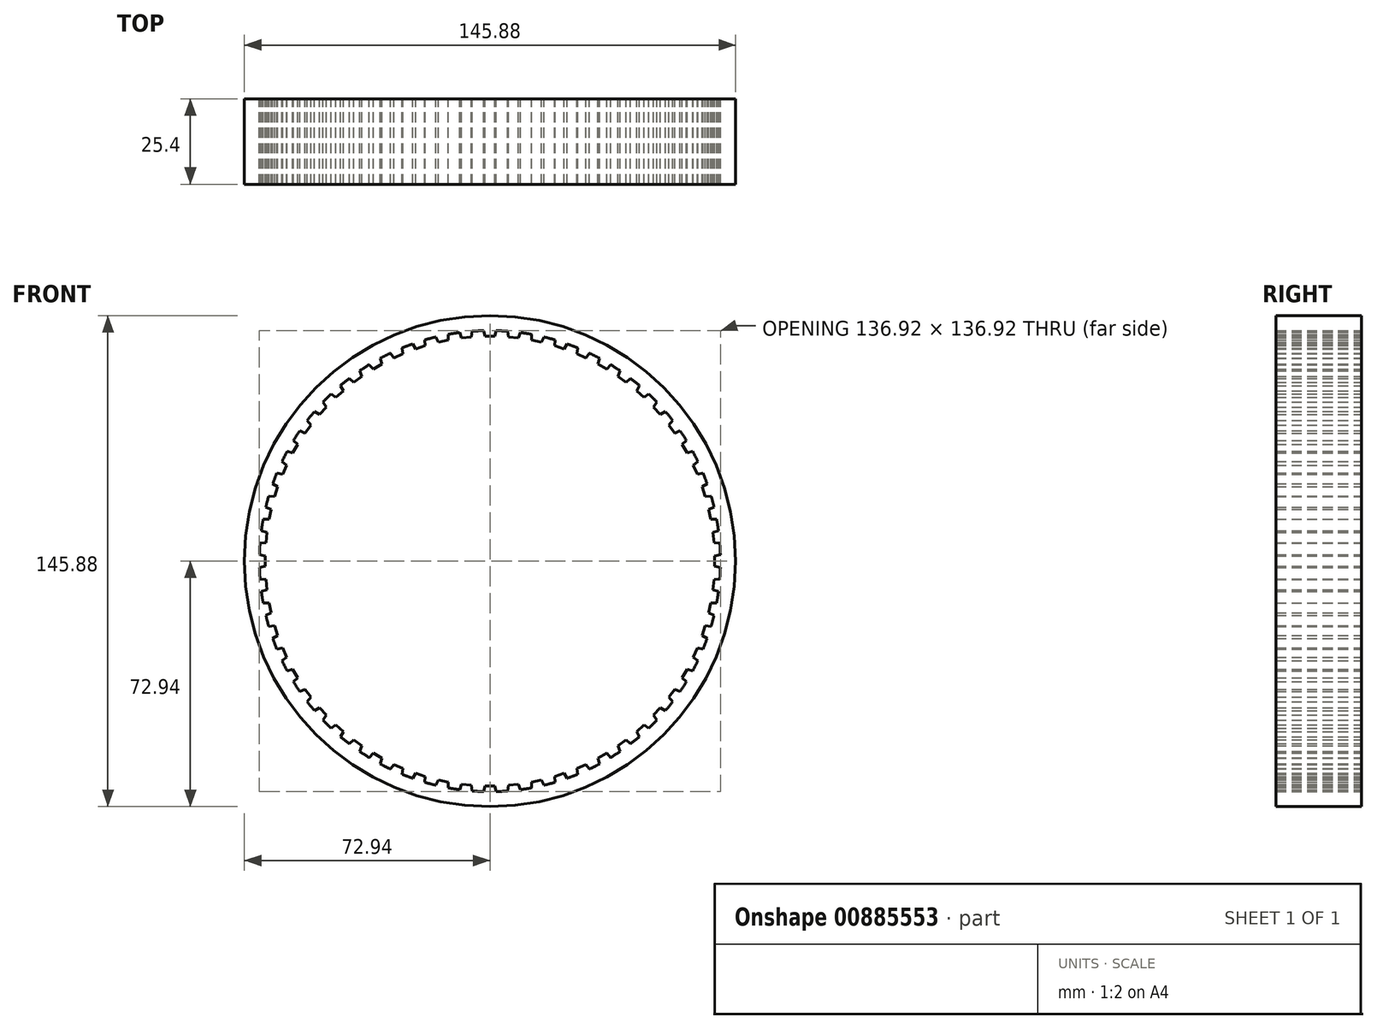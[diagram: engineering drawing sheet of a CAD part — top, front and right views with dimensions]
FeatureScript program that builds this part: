
annotation { "Feature Type Name" : "Feature", "Feature Type Description" : "" }
export const myFeature = defineFeature(function(context is Context, id is Id, definition is map)
    precondition{}
    {
        {
            var Q0;
            Q0=qCreatedBy(makeId("Front.planeOp"),FACE);
            var sketch = newSketch(context, id + "F0", { "sketchPlane" : qUnion([Q0])});
            skCircle(sketch, "E0", {"center": v(0, 0) * mm, "radius": 73.43 * mm});
            skLineSegment(sketch, "E1", {"start": v(0, 94.36) * mm, "end": v(0, -101.38) * mm, "construction": true});
            skLineSegment(sketch, "E2", {"start": v(-1.88, 68.46) * mm, "end": v(-1.48, 66.76) * mm});
            skLineSegment(sketch, "E3", {"start": v(-1.48, 66.76) * mm, "end": v(1.48, 66.76) * mm});
            skLineSegment(sketch, "E4", {"start": v(1.48, 66.76) * mm, "end": v(1.88, 68.46) * mm});
            skLineSegment(sketch, "E5", {"start": v(-8.37, 68.46) * mm, "end": v(10.76, 68.46) * mm, "construction": true});
            skLineSegment(sketch, "E6.1.0", {"start": v(-9.02, 67.89) * mm, "end": v(-8.45, 66.24) * mm});
            skLineSegment(sketch, "E6.1.1", {"start": v(-8.45, 66.24) * mm, "end": v(-5.5, 66.55) * mm});
            skLineSegment(sketch, "E6.1.2", {"start": v(-5.5, 66.55) * mm, "end": v(-5.29, 68.28) * mm});
            skLineSegment(sketch, "E6.2.0", {"start": v(-16.07, 66.57) * mm, "end": v(-15.33, 65) * mm});
            skLineSegment(sketch, "E6.2.1", {"start": v(-15.33, 65) * mm, "end": v(-12.43, 65.61) * mm});
            skLineSegment(sketch, "E6.2.2", {"start": v(-12.43, 65.61) * mm, "end": v(-12.4, 67.35) * mm});
            skLineSegment(sketch, "E7.2.3.0", {"start": v(-22.94, 64.53) * mm, "end": v(-22.04, 63.04) * mm});
            skLineSegment(sketch, "E7.3.3.0", {"start": v(-22.04, 63.04) * mm, "end": v(-19.22, 63.95) * mm});
            skLineSegment(sketch, "E7.6.3.0", {"start": v(-19.22, 63.95) * mm, "end": v(-19.37, 65.69) * mm});
            skLineSegment(sketch, "E7.2.4.0", {"start": v(-29.56, 61.78) * mm, "end": v(-28.51, 60.39) * mm});
            skLineSegment(sketch, "E7.3.4.0", {"start": v(-28.51, 60.39) * mm, "end": v(-25.8, 61.6) * mm});
            skLineSegment(sketch, "E7.6.4.0", {"start": v(-25.8, 61.6) * mm, "end": v(-26.13, 63.3) * mm});
            skLineSegment(sketch, "E7.2.5.0", {"start": v(-35.86, 58.35) * mm, "end": v(-34.67, 57.07) * mm});
            skLineSegment(sketch, "E7.3.5.0", {"start": v(-34.67, 57.07) * mm, "end": v(-32.1, 58.56) * mm});
            skLineSegment(sketch, "E7.6.5.0", {"start": v(-32.1, 58.56) * mm, "end": v(-32.6, 60.23) * mm});
            skLineSegment(sketch, "E7.2.6.0", {"start": v(-41.76, 54.28) * mm, "end": v(-40.44, 53.14) * mm});
            skLineSegment(sketch, "E7.3.6.0", {"start": v(-40.44, 53.14) * mm, "end": v(-38.04, 54.88) * mm});
            skLineSegment(sketch, "E7.6.6.0", {"start": v(-38.04, 54.88) * mm, "end": v(-38.72, 56.49) * mm});
            skLineSegment(sketch, "E7.2.7.0", {"start": v(-47.2, 49.62) * mm, "end": v(-45.77, 48.62) * mm});
            skLineSegment(sketch, "E7.3.7.0", {"start": v(-45.77, 48.62) * mm, "end": v(-43.57, 50.6) * mm});
            skLineSegment(sketch, "E7.6.7.0", {"start": v(-43.57, 50.6) * mm, "end": v(-44.41, 52.13) * mm});
            skLineSegment(sketch, "E7.2.8.0", {"start": v(-52.13, 44.41) * mm, "end": v(-50.6, 43.57) * mm});
            skLineSegment(sketch, "E7.3.8.0", {"start": v(-50.6, 43.57) * mm, "end": v(-48.62, 45.77) * mm});
            skLineSegment(sketch, "E7.6.8.0", {"start": v(-48.62, 45.77) * mm, "end": v(-49.62, 47.2) * mm});
            skLineSegment(sketch, "E7.2.9.0", {"start": v(-56.49, 38.72) * mm, "end": v(-54.88, 38.04) * mm});
            skLineSegment(sketch, "E7.3.9.0", {"start": v(-54.88, 38.04) * mm, "end": v(-53.14, 40.44) * mm});
            skLineSegment(sketch, "E7.6.9.0", {"start": v(-53.14, 40.44) * mm, "end": v(-54.28, 41.76) * mm});
            skLineSegment(sketch, "E7.2.10.0", {"start": v(-60.23, 32.6) * mm, "end": v(-58.56, 32.1) * mm});
            skLineSegment(sketch, "E7.3.10.0", {"start": v(-58.56, 32.1) * mm, "end": v(-57.07, 34.67) * mm});
            skLineSegment(sketch, "E7.6.10.0", {"start": v(-57.07, 34.67) * mm, "end": v(-58.35, 35.86) * mm});
            skLineSegment(sketch, "E7.2.11.0", {"start": v(-63.3, 26.13) * mm, "end": v(-61.6, 25.8) * mm});
            skLineSegment(sketch, "E7.3.11.0", {"start": v(-61.6, 25.8) * mm, "end": v(-60.39, 28.51) * mm});
            skLineSegment(sketch, "E7.6.11.0", {"start": v(-60.39, 28.51) * mm, "end": v(-61.78, 29.56) * mm});
            skLineSegment(sketch, "E7.2.12.0", {"start": v(-65.69, 19.37) * mm, "end": v(-63.95, 19.22) * mm});
            skLineSegment(sketch, "E7.3.12.0", {"start": v(-63.95, 19.22) * mm, "end": v(-63.04, 22.04) * mm});
            skLineSegment(sketch, "E7.6.12.0", {"start": v(-63.04, 22.04) * mm, "end": v(-64.53, 22.94) * mm});
            skLineSegment(sketch, "E7.2.13.0", {"start": v(-67.35, 12.4) * mm, "end": v(-65.61, 12.43) * mm});
            skLineSegment(sketch, "E7.3.13.0", {"start": v(-65.61, 12.43) * mm, "end": v(-65, 15.33) * mm});
            skLineSegment(sketch, "E7.6.13.0", {"start": v(-65, 15.33) * mm, "end": v(-66.57, 16.07) * mm});
            skLineSegment(sketch, "E7.2.14.0", {"start": v(-68.28, 5.29) * mm, "end": v(-66.55, 5.5) * mm});
            skLineSegment(sketch, "E7.3.14.0", {"start": v(-66.55, 5.5) * mm, "end": v(-66.24, 8.45) * mm});
            skLineSegment(sketch, "E7.6.14.0", {"start": v(-66.24, 8.45) * mm, "end": v(-67.89, 9.02) * mm});
            skLineSegment(sketch, "E7.2.15.0", {"start": v(-68.46, -1.88) * mm, "end": v(-66.76, -1.48) * mm});
            skLineSegment(sketch, "E7.3.15.0", {"start": v(-66.76, -1.48) * mm, "end": v(-66.76, 1.48) * mm});
            skLineSegment(sketch, "E7.6.15.0", {"start": v(-66.76, 1.48) * mm, "end": v(-68.46, 1.88) * mm});
            skLineSegment(sketch, "E7.2.16.0", {"start": v(-67.89, -9.02) * mm, "end": v(-66.24, -8.45) * mm});
            skLineSegment(sketch, "E7.3.16.0", {"start": v(-66.24, -8.45) * mm, "end": v(-66.55, -5.5) * mm});
            skLineSegment(sketch, "E7.6.16.0", {"start": v(-66.55, -5.5) * mm, "end": v(-68.28, -5.29) * mm});
            skLineSegment(sketch, "E7.2.17.0", {"start": v(-66.57, -16.07) * mm, "end": v(-65, -15.33) * mm});
            skLineSegment(sketch, "E7.3.17.0", {"start": v(-65, -15.33) * mm, "end": v(-65.61, -12.43) * mm});
            skLineSegment(sketch, "E7.6.17.0", {"start": v(-65.61, -12.43) * mm, "end": v(-67.35, -12.4) * mm});
            skLineSegment(sketch, "E7.2.18.0", {"start": v(-64.53, -22.94) * mm, "end": v(-63.04, -22.04) * mm});
            skLineSegment(sketch, "E7.3.18.0", {"start": v(-63.04, -22.04) * mm, "end": v(-63.95, -19.22) * mm});
            skLineSegment(sketch, "E7.6.18.0", {"start": v(-63.95, -19.22) * mm, "end": v(-65.69, -19.37) * mm});
            skLineSegment(sketch, "E7.2.19.0", {"start": v(-61.78, -29.56) * mm, "end": v(-60.39, -28.51) * mm});
            skLineSegment(sketch, "E7.3.19.0", {"start": v(-60.39, -28.51) * mm, "end": v(-61.6, -25.8) * mm});
            skLineSegment(sketch, "E7.6.19.0", {"start": v(-61.6, -25.8) * mm, "end": v(-63.3, -26.13) * mm});
            skLineSegment(sketch, "E7.2.20.0", {"start": v(-58.35, -35.86) * mm, "end": v(-57.07, -34.67) * mm});
            skLineSegment(sketch, "E7.3.20.0", {"start": v(-57.07, -34.67) * mm, "end": v(-58.56, -32.1) * mm});
            skLineSegment(sketch, "E7.6.20.0", {"start": v(-58.56, -32.1) * mm, "end": v(-60.23, -32.6) * mm});
            skLineSegment(sketch, "E7.2.21.0", {"start": v(-54.28, -41.76) * mm, "end": v(-53.14, -40.44) * mm});
            skLineSegment(sketch, "E7.3.21.0", {"start": v(-53.14, -40.44) * mm, "end": v(-54.88, -38.04) * mm});
            skLineSegment(sketch, "E7.6.21.0", {"start": v(-54.88, -38.04) * mm, "end": v(-56.49, -38.72) * mm});
            skLineSegment(sketch, "E7.2.22.0", {"start": v(-49.62, -47.2) * mm, "end": v(-48.62, -45.77) * mm});
            skLineSegment(sketch, "E7.3.22.0", {"start": v(-48.62, -45.77) * mm, "end": v(-50.6, -43.57) * mm});
            skLineSegment(sketch, "E7.6.22.0", {"start": v(-50.6, -43.57) * mm, "end": v(-52.13, -44.41) * mm});
            skLineSegment(sketch, "E7.2.23.0", {"start": v(-44.41, -52.13) * mm, "end": v(-43.57, -50.6) * mm});
            skLineSegment(sketch, "E7.3.23.0", {"start": v(-43.57, -50.6) * mm, "end": v(-45.77, -48.62) * mm});
            skLineSegment(sketch, "E7.6.23.0", {"start": v(-45.77, -48.62) * mm, "end": v(-47.2, -49.62) * mm});
            skLineSegment(sketch, "E7.2.24.0", {"start": v(-38.72, -56.49) * mm, "end": v(-38.04, -54.88) * mm});
            skLineSegment(sketch, "E7.3.24.0", {"start": v(-38.04, -54.88) * mm, "end": v(-40.44, -53.14) * mm});
            skLineSegment(sketch, "E7.6.24.0", {"start": v(-40.44, -53.14) * mm, "end": v(-41.76, -54.28) * mm});
            skLineSegment(sketch, "E7.2.25.0", {"start": v(-32.6, -60.23) * mm, "end": v(-32.1, -58.56) * mm});
            skLineSegment(sketch, "E7.3.25.0", {"start": v(-32.1, -58.56) * mm, "end": v(-34.67, -57.07) * mm});
            skLineSegment(sketch, "E7.6.25.0", {"start": v(-34.67, -57.07) * mm, "end": v(-35.86, -58.35) * mm});
            skLineSegment(sketch, "E7.2.26.0", {"start": v(-26.13, -63.3) * mm, "end": v(-25.8, -61.6) * mm});
            skLineSegment(sketch, "E7.3.26.0", {"start": v(-25.8, -61.6) * mm, "end": v(-28.51, -60.39) * mm});
            skLineSegment(sketch, "E7.6.26.0", {"start": v(-28.51, -60.39) * mm, "end": v(-29.56, -61.78) * mm});
            skLineSegment(sketch, "E7.2.27.0", {"start": v(-19.37, -65.69) * mm, "end": v(-19.22, -63.95) * mm});
            skLineSegment(sketch, "E7.3.27.0", {"start": v(-19.22, -63.95) * mm, "end": v(-22.04, -63.04) * mm});
            skLineSegment(sketch, "E7.6.27.0", {"start": v(-22.04, -63.04) * mm, "end": v(-22.94, -64.53) * mm});
            skLineSegment(sketch, "E7.2.28.0", {"start": v(-12.4, -67.35) * mm, "end": v(-12.43, -65.61) * mm});
            skLineSegment(sketch, "E7.3.28.0", {"start": v(-12.43, -65.61) * mm, "end": v(-15.33, -65) * mm});
            skLineSegment(sketch, "E7.6.28.0", {"start": v(-15.33, -65) * mm, "end": v(-16.07, -66.57) * mm});
            skLineSegment(sketch, "E7.2.29.0", {"start": v(-5.29, -68.28) * mm, "end": v(-5.5, -66.55) * mm});
            skLineSegment(sketch, "E7.3.29.0", {"start": v(-5.5, -66.55) * mm, "end": v(-8.45, -66.24) * mm});
            skLineSegment(sketch, "E7.6.29.0", {"start": v(-8.45, -66.24) * mm, "end": v(-9.02, -67.89) * mm});
            skLineSegment(sketch, "E7.2.30.0", {"start": v(1.88, -68.46) * mm, "end": v(1.48, -66.76) * mm});
            skLineSegment(sketch, "E7.3.30.0", {"start": v(1.48, -66.76) * mm, "end": v(-1.48, -66.76) * mm});
            skLineSegment(sketch, "E7.6.30.0", {"start": v(-1.48, -66.76) * mm, "end": v(-1.88, -68.46) * mm});
            skLineSegment(sketch, "E7.2.31.0", {"start": v(9.02, -67.89) * mm, "end": v(8.45, -66.24) * mm});
            skLineSegment(sketch, "E7.3.31.0", {"start": v(8.45, -66.24) * mm, "end": v(5.5, -66.55) * mm});
            skLineSegment(sketch, "E7.6.31.0", {"start": v(5.5, -66.55) * mm, "end": v(5.29, -68.28) * mm});
            skLineSegment(sketch, "E7.2.32.0", {"start": v(16.07, -66.57) * mm, "end": v(15.33, -65) * mm});
            skLineSegment(sketch, "E7.3.32.0", {"start": v(15.33, -65) * mm, "end": v(12.43, -65.61) * mm});
            skLineSegment(sketch, "E7.6.32.0", {"start": v(12.43, -65.61) * mm, "end": v(12.4, -67.35) * mm});
            skLineSegment(sketch, "E7.2.33.0", {"start": v(22.94, -64.53) * mm, "end": v(22.04, -63.04) * mm});
            skLineSegment(sketch, "E7.3.33.0", {"start": v(22.04, -63.04) * mm, "end": v(19.22, -63.95) * mm});
            skLineSegment(sketch, "E7.6.33.0", {"start": v(19.22, -63.95) * mm, "end": v(19.37, -65.69) * mm});
            skLineSegment(sketch, "E7.2.34.0", {"start": v(29.56, -61.78) * mm, "end": v(28.51, -60.39) * mm});
            skLineSegment(sketch, "E7.3.34.0", {"start": v(28.51, -60.39) * mm, "end": v(25.8, -61.6) * mm});
            skLineSegment(sketch, "E7.6.34.0", {"start": v(25.8, -61.6) * mm, "end": v(26.13, -63.3) * mm});
            skLineSegment(sketch, "E7.2.35.0", {"start": v(35.86, -58.35) * mm, "end": v(34.67, -57.07) * mm});
            skLineSegment(sketch, "E7.3.35.0", {"start": v(34.67, -57.07) * mm, "end": v(32.1, -58.56) * mm});
            skLineSegment(sketch, "E7.6.35.0", {"start": v(32.1, -58.56) * mm, "end": v(32.6, -60.23) * mm});
            skLineSegment(sketch, "E7.2.36.0", {"start": v(41.76, -54.28) * mm, "end": v(40.44, -53.14) * mm});
            skLineSegment(sketch, "E7.3.36.0", {"start": v(40.44, -53.14) * mm, "end": v(38.04, -54.88) * mm});
            skLineSegment(sketch, "E7.6.36.0", {"start": v(38.04, -54.88) * mm, "end": v(38.72, -56.49) * mm});
            skLineSegment(sketch, "E7.2.37.0", {"start": v(47.2, -49.62) * mm, "end": v(45.77, -48.62) * mm});
            skLineSegment(sketch, "E7.3.37.0", {"start": v(45.77, -48.62) * mm, "end": v(43.57, -50.6) * mm});
            skLineSegment(sketch, "E7.6.37.0", {"start": v(43.57, -50.6) * mm, "end": v(44.41, -52.13) * mm});
            skLineSegment(sketch, "E7.2.38.0", {"start": v(52.13, -44.41) * mm, "end": v(50.6, -43.57) * mm});
            skLineSegment(sketch, "E7.3.38.0", {"start": v(50.6, -43.57) * mm, "end": v(48.62, -45.77) * mm});
            skLineSegment(sketch, "E7.6.38.0", {"start": v(48.62, -45.77) * mm, "end": v(49.62, -47.2) * mm});
            skLineSegment(sketch, "E7.2.39.0", {"start": v(56.49, -38.72) * mm, "end": v(54.88, -38.04) * mm});
            skLineSegment(sketch, "E7.3.39.0", {"start": v(54.88, -38.04) * mm, "end": v(53.14, -40.44) * mm});
            skLineSegment(sketch, "E7.6.39.0", {"start": v(53.14, -40.44) * mm, "end": v(54.28, -41.76) * mm});
            skLineSegment(sketch, "E7.2.40.0", {"start": v(60.23, -32.6) * mm, "end": v(58.56, -32.1) * mm});
            skLineSegment(sketch, "E7.3.40.0", {"start": v(58.56, -32.1) * mm, "end": v(57.07, -34.67) * mm});
            skLineSegment(sketch, "E7.6.40.0", {"start": v(57.07, -34.67) * mm, "end": v(58.35, -35.86) * mm});
            skLineSegment(sketch, "E7.2.41.0", {"start": v(63.3, -26.13) * mm, "end": v(61.6, -25.8) * mm});
            skLineSegment(sketch, "E7.3.41.0", {"start": v(61.6, -25.8) * mm, "end": v(60.39, -28.51) * mm});
            skLineSegment(sketch, "E7.6.41.0", {"start": v(60.39, -28.51) * mm, "end": v(61.78, -29.56) * mm});
            skLineSegment(sketch, "E7.2.42.0", {"start": v(65.69, -19.37) * mm, "end": v(63.95, -19.22) * mm});
            skLineSegment(sketch, "E7.3.42.0", {"start": v(63.95, -19.22) * mm, "end": v(63.04, -22.04) * mm});
            skLineSegment(sketch, "E7.6.42.0", {"start": v(63.04, -22.04) * mm, "end": v(64.53, -22.94) * mm});
            skLineSegment(sketch, "E7.2.43.0", {"start": v(67.35, -12.4) * mm, "end": v(65.61, -12.43) * mm});
            skLineSegment(sketch, "E7.3.43.0", {"start": v(65.61, -12.43) * mm, "end": v(65, -15.33) * mm});
            skLineSegment(sketch, "E7.6.43.0", {"start": v(65, -15.33) * mm, "end": v(66.57, -16.07) * mm});
            skLineSegment(sketch, "E7.2.44.0", {"start": v(68.28, -5.29) * mm, "end": v(66.55, -5.5) * mm});
            skLineSegment(sketch, "E7.3.44.0", {"start": v(66.55, -5.5) * mm, "end": v(66.24, -8.45) * mm});
            skLineSegment(sketch, "E7.6.44.0", {"start": v(66.24, -8.45) * mm, "end": v(67.89, -9.02) * mm});
            skLineSegment(sketch, "E7.2.45.0", {"start": v(68.46, 1.88) * mm, "end": v(66.76, 1.48) * mm});
            skLineSegment(sketch, "E7.3.45.0", {"start": v(66.76, 1.48) * mm, "end": v(66.76, -1.48) * mm});
            skLineSegment(sketch, "E7.6.45.0", {"start": v(66.76, -1.48) * mm, "end": v(68.46, -1.88) * mm});
            skLineSegment(sketch, "E7.2.46.0", {"start": v(67.89, 9.02) * mm, "end": v(66.24, 8.45) * mm});
            skLineSegment(sketch, "E7.3.46.0", {"start": v(66.24, 8.45) * mm, "end": v(66.55, 5.5) * mm});
            skLineSegment(sketch, "E7.6.46.0", {"start": v(66.55, 5.5) * mm, "end": v(68.28, 5.29) * mm});
            skLineSegment(sketch, "E7.2.47.0", {"start": v(66.57, 16.07) * mm, "end": v(65, 15.33) * mm});
            skLineSegment(sketch, "E7.3.47.0", {"start": v(65, 15.33) * mm, "end": v(65.61, 12.43) * mm});
            skLineSegment(sketch, "E7.6.47.0", {"start": v(65.61, 12.43) * mm, "end": v(67.35, 12.4) * mm});
            skLineSegment(sketch, "E7.2.48.0", {"start": v(64.53, 22.94) * mm, "end": v(63.04, 22.04) * mm});
            skLineSegment(sketch, "E7.3.48.0", {"start": v(63.04, 22.04) * mm, "end": v(63.95, 19.22) * mm});
            skLineSegment(sketch, "E7.6.48.0", {"start": v(63.95, 19.22) * mm, "end": v(65.69, 19.37) * mm});
            skLineSegment(sketch, "E7.2.49.0", {"start": v(61.78, 29.56) * mm, "end": v(60.39, 28.51) * mm});
            skLineSegment(sketch, "E7.3.49.0", {"start": v(60.39, 28.51) * mm, "end": v(61.6, 25.8) * mm});
            skLineSegment(sketch, "E7.6.49.0", {"start": v(61.6, 25.8) * mm, "end": v(63.3, 26.13) * mm});
            skLineSegment(sketch, "E8.2.50.0", {"start": v(58.35, 35.86) * mm, "end": v(57.07, 34.67) * mm});
            skLineSegment(sketch, "E8.3.50.0", {"start": v(57.07, 34.67) * mm, "end": v(58.56, 32.1) * mm});
            skLineSegment(sketch, "E8.6.50.0", {"start": v(58.56, 32.1) * mm, "end": v(60.23, 32.6) * mm});
            skLineSegment(sketch, "E8.2.51.0", {"start": v(54.28, 41.76) * mm, "end": v(53.14, 40.44) * mm});
            skLineSegment(sketch, "E8.3.51.0", {"start": v(53.14, 40.44) * mm, "end": v(54.88, 38.04) * mm});
            skLineSegment(sketch, "E8.6.51.0", {"start": v(54.88, 38.04) * mm, "end": v(56.49, 38.72) * mm});
            skLineSegment(sketch, "E8.2.52.0", {"start": v(49.62, 47.2) * mm, "end": v(48.62, 45.77) * mm});
            skLineSegment(sketch, "E8.3.52.0", {"start": v(48.62, 45.77) * mm, "end": v(50.6, 43.57) * mm});
            skLineSegment(sketch, "E8.6.52.0", {"start": v(50.6, 43.57) * mm, "end": v(52.13, 44.41) * mm});
            skLineSegment(sketch, "E8.2.53.0", {"start": v(44.41, 52.13) * mm, "end": v(43.57, 50.6) * mm});
            skLineSegment(sketch, "E8.3.53.0", {"start": v(43.57, 50.6) * mm, "end": v(45.77, 48.62) * mm});
            skLineSegment(sketch, "E8.6.53.0", {"start": v(45.77, 48.62) * mm, "end": v(47.2, 49.62) * mm});
            skLineSegment(sketch, "E8.2.54.0", {"start": v(38.72, 56.49) * mm, "end": v(38.04, 54.88) * mm});
            skLineSegment(sketch, "E8.3.54.0", {"start": v(38.04, 54.88) * mm, "end": v(40.44, 53.14) * mm});
            skLineSegment(sketch, "E8.6.54.0", {"start": v(40.44, 53.14) * mm, "end": v(41.76, 54.28) * mm});
            skLineSegment(sketch, "E8.2.55.0", {"start": v(32.6, 60.23) * mm, "end": v(32.1, 58.56) * mm});
            skLineSegment(sketch, "E8.3.55.0", {"start": v(32.1, 58.56) * mm, "end": v(34.67, 57.07) * mm});
            skLineSegment(sketch, "E8.6.55.0", {"start": v(34.67, 57.07) * mm, "end": v(35.86, 58.35) * mm});
            skLineSegment(sketch, "E8.2.56.0", {"start": v(26.13, 63.3) * mm, "end": v(25.8, 61.6) * mm});
            skLineSegment(sketch, "E8.3.56.0", {"start": v(25.8, 61.6) * mm, "end": v(28.51, 60.39) * mm});
            skLineSegment(sketch, "E8.6.56.0", {"start": v(28.51, 60.39) * mm, "end": v(29.56, 61.78) * mm});
            skLineSegment(sketch, "E8.2.57.0", {"start": v(19.37, 65.69) * mm, "end": v(19.22, 63.95) * mm});
            skLineSegment(sketch, "E8.3.57.0", {"start": v(19.22, 63.95) * mm, "end": v(22.04, 63.04) * mm});
            skLineSegment(sketch, "E8.6.57.0", {"start": v(22.04, 63.04) * mm, "end": v(22.94, 64.53) * mm});
            skLineSegment(sketch, "E8.2.58.0", {"start": v(12.4, 67.35) * mm, "end": v(12.43, 65.61) * mm});
            skLineSegment(sketch, "E8.3.58.0", {"start": v(12.43, 65.61) * mm, "end": v(15.33, 65) * mm});
            skLineSegment(sketch, "E8.6.58.0", {"start": v(15.33, 65) * mm, "end": v(16.07, 66.57) * mm});
            skLineSegment(sketch, "E8.2.59.0", {"start": v(5.29, 68.28) * mm, "end": v(5.5, 66.55) * mm});
            skLineSegment(sketch, "E8.3.59.0", {"start": v(5.5, 66.55) * mm, "end": v(8.45, 66.24) * mm});
            skLineSegment(sketch, "E8.6.59.0", {"start": v(8.45, 66.24) * mm, "end": v(9.02, 67.89) * mm});
            skLineSegment(sketch, "E9.1.0", {"start": v(-56.74, -42.42) * mm, "end": v(-66.3, -25.86) * mm, "construction": true});
            skLineSegment(sketch, "E9.2.0", {"start": v(65.11, -27.93) * mm, "end": v(55.55, -44.5) * mm, "construction": true});
            skCircle(sketch, "E10", {"center": v(0, 0) * mm, "radius": 68.49 * mm});
            skSolve(sketch);
        }
        {
            var Q0;
            {var subQ78=sQuery(id+"F0.wireOp",EDGE,"E2");Q0=makeQuery(id+"F0.imprint","IMPRINT",FACE,{"disambiguationData":[TD([[makeQuery(id+"F0.imprint","IMPRINT",EDGE,{"derivedFrom":subQ78}),-1.0]])]});}
            extrude(context, id + "F1", {"entities" : qUnion([Q0]), "depth" : 25.4 * mm, "offsetDistance" : 25.4 * mm});
        }
        {
            var Q0;
            Q0=makeQuery(id+"F1.opExtrude","CAP_FACE",FACE,{"disambiguationData":[OSD([sQuery(id+"F0.wireOp",EDGE,"E2"),sQuery(id+"F0.wireOp",EDGE,"E3"),sQuery(id+"F0.wireOp",EDGE,"E4"),sQuery(id+"F0.wireOp",EDGE,"E6.1.0"),sQuery(id+"F0.wireOp",EDGE,"E6.1.1"),sQuery(id+"F0.wireOp",EDGE,"E6.1.2"),sQuery(id+"F0.wireOp",EDGE,"E6.2.0"),sQuery(id+"F0.wireOp",EDGE,"E6.2.1"),sQuery(id+"F0.wireOp",EDGE,"E6.2.2"),sQuery(id+"F0.wireOp",EDGE,"E7.2.3.0"),sQuery(id+"F0.wireOp",EDGE,"E7.3.3.0"),sQuery(id+"F0.wireOp",EDGE,"E7.6.3.0"),sQuery(id+"F0.wireOp",EDGE,"E7.2.4.0"),sQuery(id+"F0.wireOp",EDGE,"E7.3.4.0"),sQuery(id+"F0.wireOp",EDGE,"E7.6.4.0"),sQuery(id+"F0.wireOp",EDGE,"E7.2.5.0"),sQuery(id+"F0.wireOp",EDGE,"E7.3.5.0"),sQuery(id+"F0.wireOp",EDGE,"E7.6.5.0"),sQuery(id+"F0.wireOp",EDGE,"E7.2.6.0"),sQuery(id+"F0.wireOp",EDGE,"E7.3.6.0"),sQuery(id+"F0.wireOp",EDGE,"E7.6.6.0"),sQuery(id+"F0.wireOp",EDGE,"E7.2.7.0"),sQuery(id+"F0.wireOp",EDGE,"E7.3.7.0"),sQuery(id+"F0.wireOp",EDGE,"E7.6.7.0"),sQuery(id+"F0.wireOp",EDGE,"E7.2.8.0"),sQuery(id+"F0.wireOp",EDGE,"E7.3.8.0"),sQuery(id+"F0.wireOp",EDGE,"E7.6.8.0"),sQuery(id+"F0.wireOp",EDGE,"E7.2.9.0"),sQuery(id+"F0.wireOp",EDGE,"E7.3.9.0"),sQuery(id+"F0.wireOp",EDGE,"E7.6.9.0"),sQuery(id+"F0.wireOp",EDGE,"E7.2.10.0"),sQuery(id+"F0.wireOp",EDGE,"E7.3.10.0"),sQuery(id+"F0.wireOp",EDGE,"E7.6.10.0"),sQuery(id+"F0.wireOp",EDGE,"E7.2.11.0"),sQuery(id+"F0.wireOp",EDGE,"E7.3.11.0"),sQuery(id+"F0.wireOp",EDGE,"E7.6.11.0"),sQuery(id+"F0.wireOp",EDGE,"E7.2.12.0"),sQuery(id+"F0.wireOp",EDGE,"E7.3.12.0"),sQuery(id+"F0.wireOp",EDGE,"E7.6.12.0"),sQuery(id+"F0.wireOp",EDGE,"E7.2.13.0"),sQuery(id+"F0.wireOp",EDGE,"E7.3.13.0"),sQuery(id+"F0.wireOp",EDGE,"E7.6.13.0"),sQuery(id+"F0.wireOp",EDGE,"E7.2.14.0"),sQuery(id+"F0.wireOp",EDGE,"E7.3.14.0"),sQuery(id+"F0.wireOp",EDGE,"E7.6.14.0"),sQuery(id+"F0.wireOp",EDGE,"E7.2.15.0"),sQuery(id+"F0.wireOp",EDGE,"E7.3.15.0"),sQuery(id+"F0.wireOp",EDGE,"E7.6.15.0"),sQuery(id+"F0.wireOp",EDGE,"E7.2.16.0"),sQuery(id+"F0.wireOp",EDGE,"E7.3.16.0"),sQuery(id+"F0.wireOp",EDGE,"E7.6.16.0"),sQuery(id+"F0.wireOp",EDGE,"E7.2.17.0"),sQuery(id+"F0.wireOp",EDGE,"E7.3.17.0"),sQuery(id+"F0.wireOp",EDGE,"E7.6.17.0"),sQuery(id+"F0.wireOp",EDGE,"E7.2.18.0"),sQuery(id+"F0.wireOp",EDGE,"E7.3.18.0"),sQuery(id+"F0.wireOp",EDGE,"E7.6.18.0"),sQuery(id+"F0.wireOp",EDGE,"E7.2.19.0"),sQuery(id+"F0.wireOp",EDGE,"E7.3.19.0"),sQuery(id+"F0.wireOp",EDGE,"E7.6.19.0"),sQuery(id+"F0.wireOp",EDGE,"E7.2.20.0"),sQuery(id+"F0.wireOp",EDGE,"E7.3.20.0"),sQuery(id+"F0.wireOp",EDGE,"E7.6.20.0"),sQuery(id+"F0.wireOp",EDGE,"E7.2.21.0"),sQuery(id+"F0.wireOp",EDGE,"E7.3.21.0"),sQuery(id+"F0.wireOp",EDGE,"E7.6.21.0"),sQuery(id+"F0.wireOp",EDGE,"E7.2.22.0"),sQuery(id+"F0.wireOp",EDGE,"E7.3.22.0"),sQuery(id+"F0.wireOp",EDGE,"E7.6.22.0"),sQuery(id+"F0.wireOp",EDGE,"E7.2.23.0"),sQuery(id+"F0.wireOp",EDGE,"E7.3.23.0"),sQuery(id+"F0.wireOp",EDGE,"E7.6.23.0"),sQuery(id+"F0.wireOp",EDGE,"E7.2.24.0"),sQuery(id+"F0.wireOp",EDGE,"E7.3.24.0"),sQuery(id+"F0.wireOp",EDGE,"E7.6.24.0"),sQuery(id+"F0.wireOp",EDGE,"E7.2.25.0"),sQuery(id+"F0.wireOp",EDGE,"E7.3.25.0"),sQuery(id+"F0.wireOp",EDGE,"E7.6.25.0"),sQuery(id+"F0.wireOp",EDGE,"E7.2.26.0"),sQuery(id+"F0.wireOp",EDGE,"E7.3.26.0"),sQuery(id+"F0.wireOp",EDGE,"E7.6.26.0"),sQuery(id+"F0.wireOp",EDGE,"E7.2.27.0"),sQuery(id+"F0.wireOp",EDGE,"E7.3.27.0"),sQuery(id+"F0.wireOp",EDGE,"E7.6.27.0"),sQuery(id+"F0.wireOp",EDGE,"E7.2.28.0"),sQuery(id+"F0.wireOp",EDGE,"E7.3.28.0"),sQuery(id+"F0.wireOp",EDGE,"E7.6.28.0"),sQuery(id+"F0.wireOp",EDGE,"E7.2.29.0"),sQuery(id+"F0.wireOp",EDGE,"E7.3.29.0"),sQuery(id+"F0.wireOp",EDGE,"E7.6.29.0"),sQuery(id+"F0.wireOp",EDGE,"E7.2.30.0"),sQuery(id+"F0.wireOp",EDGE,"E7.3.30.0"),sQuery(id+"F0.wireOp",EDGE,"E7.6.30.0"),sQuery(id+"F0.wireOp",EDGE,"E7.2.31.0"),sQuery(id+"F0.wireOp",EDGE,"E7.3.31.0"),sQuery(id+"F0.wireOp",EDGE,"E7.6.31.0"),sQuery(id+"F0.wireOp",EDGE,"E7.2.32.0"),sQuery(id+"F0.wireOp",EDGE,"E7.3.32.0"),sQuery(id+"F0.wireOp",EDGE,"E7.6.32.0"),sQuery(id+"F0.wireOp",EDGE,"E7.2.33.0"),sQuery(id+"F0.wireOp",EDGE,"E7.3.33.0"),sQuery(id+"F0.wireOp",EDGE,"E7.6.33.0"),sQuery(id+"F0.wireOp",EDGE,"E7.2.34.0"),sQuery(id+"F0.wireOp",EDGE,"E7.3.34.0"),sQuery(id+"F0.wireOp",EDGE,"E7.6.34.0"),sQuery(id+"F0.wireOp",EDGE,"E7.2.35.0"),sQuery(id+"F0.wireOp",EDGE,"E7.3.35.0"),sQuery(id+"F0.wireOp",EDGE,"E7.6.35.0"),sQuery(id+"F0.wireOp",EDGE,"E7.2.36.0"),sQuery(id+"F0.wireOp",EDGE,"E7.3.36.0"),sQuery(id+"F0.wireOp",EDGE,"E7.6.36.0"),sQuery(id+"F0.wireOp",EDGE,"E7.2.37.0"),sQuery(id+"F0.wireOp",EDGE,"E7.3.37.0"),sQuery(id+"F0.wireOp",EDGE,"E7.6.37.0"),sQuery(id+"F0.wireOp",EDGE,"E7.2.38.0"),sQuery(id+"F0.wireOp",EDGE,"E7.3.38.0"),sQuery(id+"F0.wireOp",EDGE,"E7.6.38.0"),sQuery(id+"F0.wireOp",EDGE,"E7.2.39.0"),sQuery(id+"F0.wireOp",EDGE,"E7.3.39.0"),sQuery(id+"F0.wireOp",EDGE,"E7.6.39.0"),sQuery(id+"F0.wireOp",EDGE,"E7.2.40.0"),sQuery(id+"F0.wireOp",EDGE,"E7.3.40.0"),sQuery(id+"F0.wireOp",EDGE,"E7.6.40.0"),sQuery(id+"F0.wireOp",EDGE,"E7.2.41.0"),sQuery(id+"F0.wireOp",EDGE,"E7.3.41.0"),sQuery(id+"F0.wireOp",EDGE,"E7.6.41.0"),sQuery(id+"F0.wireOp",EDGE,"E7.2.42.0"),sQuery(id+"F0.wireOp",EDGE,"E7.3.42.0"),sQuery(id+"F0.wireOp",EDGE,"E7.6.42.0"),sQuery(id+"F0.wireOp",EDGE,"E7.2.43.0"),sQuery(id+"F0.wireOp",EDGE,"E7.3.43.0"),sQuery(id+"F0.wireOp",EDGE,"E7.6.43.0"),sQuery(id+"F0.wireOp",EDGE,"E7.2.44.0"),sQuery(id+"F0.wireOp",EDGE,"E7.3.44.0"),sQuery(id+"F0.wireOp",EDGE,"E7.6.44.0"),sQuery(id+"F0.wireOp",EDGE,"E7.2.45.0"),sQuery(id+"F0.wireOp",EDGE,"E7.3.45.0"),sQuery(id+"F0.wireOp",EDGE,"E7.6.45.0"),sQuery(id+"F0.wireOp",EDGE,"E7.2.46.0"),sQuery(id+"F0.wireOp",EDGE,"E7.3.46.0"),sQuery(id+"F0.wireOp",EDGE,"E7.6.46.0"),sQuery(id+"F0.wireOp",EDGE,"E7.2.47.0"),sQuery(id+"F0.wireOp",EDGE,"E7.3.47.0"),sQuery(id+"F0.wireOp",EDGE,"E7.6.47.0"),sQuery(id+"F0.wireOp",EDGE,"E7.2.48.0"),sQuery(id+"F0.wireOp",EDGE,"E7.3.48.0"),sQuery(id+"F0.wireOp",EDGE,"E7.6.48.0"),sQuery(id+"F0.wireOp",EDGE,"E7.2.49.0"),sQuery(id+"F0.wireOp",EDGE,"E7.3.49.0"),sQuery(id+"F0.wireOp",EDGE,"E7.6.49.0"),sQuery(id+"F0.wireOp",EDGE,"E8.2.50.0"),sQuery(id+"F0.wireOp",EDGE,"E8.3.50.0"),sQuery(id+"F0.wireOp",EDGE,"E8.6.50.0"),sQuery(id+"F0.wireOp",EDGE,"E8.2.51.0"),sQuery(id+"F0.wireOp",EDGE,"E8.3.51.0"),sQuery(id+"F0.wireOp",EDGE,"E8.6.51.0"),sQuery(id+"F0.wireOp",EDGE,"E8.2.52.0"),sQuery(id+"F0.wireOp",EDGE,"E8.3.52.0"),sQuery(id+"F0.wireOp",EDGE,"E8.6.52.0"),sQuery(id+"F0.wireOp",EDGE,"E8.2.53.0"),sQuery(id+"F0.wireOp",EDGE,"E8.3.53.0"),sQuery(id+"F0.wireOp",EDGE,"E8.6.53.0"),sQuery(id+"F0.wireOp",EDGE,"E8.2.54.0"),sQuery(id+"F0.wireOp",EDGE,"E8.3.54.0"),sQuery(id+"F0.wireOp",EDGE,"E8.6.54.0"),sQuery(id+"F0.wireOp",EDGE,"E8.2.55.0"),sQuery(id+"F0.wireOp",EDGE,"E8.3.55.0"),sQuery(id+"F0.wireOp",EDGE,"E8.6.55.0"),sQuery(id+"F0.wireOp",EDGE,"E8.2.56.0"),sQuery(id+"F0.wireOp",EDGE,"E8.3.56.0"),sQuery(id+"F0.wireOp",EDGE,"E8.6.56.0"),sQuery(id+"F0.wireOp",EDGE,"E8.2.57.0"),sQuery(id+"F0.wireOp",EDGE,"E8.3.57.0"),sQuery(id+"F0.wireOp",EDGE,"E8.6.57.0"),sQuery(id+"F0.wireOp",EDGE,"E8.2.58.0"),sQuery(id+"F0.wireOp",EDGE,"E8.3.58.0"),sQuery(id+"F0.wireOp",EDGE,"E8.6.58.0"),sQuery(id+"F0.wireOp",EDGE,"E8.2.59.0"),sQuery(id+"F0.wireOp",EDGE,"E8.3.59.0"),sQuery(id+"F0.wireOp",EDGE,"E8.6.59.0"),sQuery(id+"F0.wireOp",EDGE,"E10")])],"isStart":false});
            var sketch = newSketch(context, id + "F2", { "sketchPlane" : qUnion([Q0])});
            skCircle(sketch, "E11", {"center": v(0, 0) * mm, "radius": 72.94 * mm});
            skSolve(sketch);
        }
        {
            var Q0;
            Q0=makeQuery(id+"F2.imprint","IMPRINT",FACE,{"disambiguationData":[TD([[makeQuery(id+"F2.imprint","IMPRINT",EDGE,{"derivedFrom":sQuery(id+"F2.wireOp",EDGE,"E11")}),1.0]])]});
            extrude(context, id + "F3", {"entities" : qUnion([Q0]), "operationType" : NewBodyOperationType.ADD, "depth" : 25.4 * mm, "offsetDistance" : 25.4 * mm});
        }
        {
            var Q0;
            Q0=makeQuery(id+"F1.opExtrude","CAP_FACE",FACE,{"disambiguationData":[OSD([sQuery(id+"F0.wireOp",EDGE,"E2"),sQuery(id+"F0.wireOp",EDGE,"E3"),sQuery(id+"F0.wireOp",EDGE,"E4"),sQuery(id+"F0.wireOp",EDGE,"E6.1.0"),sQuery(id+"F0.wireOp",EDGE,"E6.1.1"),sQuery(id+"F0.wireOp",EDGE,"E6.1.2"),sQuery(id+"F0.wireOp",EDGE,"E6.2.0"),sQuery(id+"F0.wireOp",EDGE,"E6.2.1"),sQuery(id+"F0.wireOp",EDGE,"E6.2.2"),sQuery(id+"F0.wireOp",EDGE,"E7.2.3.0"),sQuery(id+"F0.wireOp",EDGE,"E7.3.3.0"),sQuery(id+"F0.wireOp",EDGE,"E7.6.3.0"),sQuery(id+"F0.wireOp",EDGE,"E7.2.4.0"),sQuery(id+"F0.wireOp",EDGE,"E7.3.4.0"),sQuery(id+"F0.wireOp",EDGE,"E7.6.4.0"),sQuery(id+"F0.wireOp",EDGE,"E7.2.5.0"),sQuery(id+"F0.wireOp",EDGE,"E7.3.5.0"),sQuery(id+"F0.wireOp",EDGE,"E7.6.5.0"),sQuery(id+"F0.wireOp",EDGE,"E7.2.6.0"),sQuery(id+"F0.wireOp",EDGE,"E7.3.6.0"),sQuery(id+"F0.wireOp",EDGE,"E7.6.6.0"),sQuery(id+"F0.wireOp",EDGE,"E7.2.7.0"),sQuery(id+"F0.wireOp",EDGE,"E7.3.7.0"),sQuery(id+"F0.wireOp",EDGE,"E7.6.7.0"),sQuery(id+"F0.wireOp",EDGE,"E7.2.8.0"),sQuery(id+"F0.wireOp",EDGE,"E7.3.8.0"),sQuery(id+"F0.wireOp",EDGE,"E7.6.8.0"),sQuery(id+"F0.wireOp",EDGE,"E7.2.9.0"),sQuery(id+"F0.wireOp",EDGE,"E7.3.9.0"),sQuery(id+"F0.wireOp",EDGE,"E7.6.9.0"),sQuery(id+"F0.wireOp",EDGE,"E7.2.10.0"),sQuery(id+"F0.wireOp",EDGE,"E7.3.10.0"),sQuery(id+"F0.wireOp",EDGE,"E7.6.10.0"),sQuery(id+"F0.wireOp",EDGE,"E7.2.11.0"),sQuery(id+"F0.wireOp",EDGE,"E7.3.11.0"),sQuery(id+"F0.wireOp",EDGE,"E7.6.11.0"),sQuery(id+"F0.wireOp",EDGE,"E7.2.12.0"),sQuery(id+"F0.wireOp",EDGE,"E7.3.12.0"),sQuery(id+"F0.wireOp",EDGE,"E7.6.12.0"),sQuery(id+"F0.wireOp",EDGE,"E7.2.13.0"),sQuery(id+"F0.wireOp",EDGE,"E7.3.13.0"),sQuery(id+"F0.wireOp",EDGE,"E7.6.13.0"),sQuery(id+"F0.wireOp",EDGE,"E7.2.14.0"),sQuery(id+"F0.wireOp",EDGE,"E7.3.14.0"),sQuery(id+"F0.wireOp",EDGE,"E7.6.14.0"),sQuery(id+"F0.wireOp",EDGE,"E7.2.15.0"),sQuery(id+"F0.wireOp",EDGE,"E7.3.15.0"),sQuery(id+"F0.wireOp",EDGE,"E7.6.15.0"),sQuery(id+"F0.wireOp",EDGE,"E7.2.16.0"),sQuery(id+"F0.wireOp",EDGE,"E7.3.16.0"),sQuery(id+"F0.wireOp",EDGE,"E7.6.16.0"),sQuery(id+"F0.wireOp",EDGE,"E7.2.17.0"),sQuery(id+"F0.wireOp",EDGE,"E7.3.17.0"),sQuery(id+"F0.wireOp",EDGE,"E7.6.17.0"),sQuery(id+"F0.wireOp",EDGE,"E7.2.18.0"),sQuery(id+"F0.wireOp",EDGE,"E7.3.18.0"),sQuery(id+"F0.wireOp",EDGE,"E7.6.18.0"),sQuery(id+"F0.wireOp",EDGE,"E7.2.19.0"),sQuery(id+"F0.wireOp",EDGE,"E7.3.19.0"),sQuery(id+"F0.wireOp",EDGE,"E7.6.19.0"),sQuery(id+"F0.wireOp",EDGE,"E7.2.20.0"),sQuery(id+"F0.wireOp",EDGE,"E7.3.20.0"),sQuery(id+"F0.wireOp",EDGE,"E7.6.20.0"),sQuery(id+"F0.wireOp",EDGE,"E7.2.21.0"),sQuery(id+"F0.wireOp",EDGE,"E7.3.21.0"),sQuery(id+"F0.wireOp",EDGE,"E7.6.21.0"),sQuery(id+"F0.wireOp",EDGE,"E7.2.22.0"),sQuery(id+"F0.wireOp",EDGE,"E7.3.22.0"),sQuery(id+"F0.wireOp",EDGE,"E7.6.22.0"),sQuery(id+"F0.wireOp",EDGE,"E7.2.23.0"),sQuery(id+"F0.wireOp",EDGE,"E7.3.23.0"),sQuery(id+"F0.wireOp",EDGE,"E7.6.23.0"),sQuery(id+"F0.wireOp",EDGE,"E7.2.24.0"),sQuery(id+"F0.wireOp",EDGE,"E7.3.24.0"),sQuery(id+"F0.wireOp",EDGE,"E7.6.24.0"),sQuery(id+"F0.wireOp",EDGE,"E7.2.25.0"),sQuery(id+"F0.wireOp",EDGE,"E7.3.25.0"),sQuery(id+"F0.wireOp",EDGE,"E7.6.25.0"),sQuery(id+"F0.wireOp",EDGE,"E7.2.26.0"),sQuery(id+"F0.wireOp",EDGE,"E7.3.26.0"),sQuery(id+"F0.wireOp",EDGE,"E7.6.26.0"),sQuery(id+"F0.wireOp",EDGE,"E7.2.27.0"),sQuery(id+"F0.wireOp",EDGE,"E7.3.27.0"),sQuery(id+"F0.wireOp",EDGE,"E7.6.27.0"),sQuery(id+"F0.wireOp",EDGE,"E7.2.28.0"),sQuery(id+"F0.wireOp",EDGE,"E7.3.28.0"),sQuery(id+"F0.wireOp",EDGE,"E7.6.28.0"),sQuery(id+"F0.wireOp",EDGE,"E7.2.29.0"),sQuery(id+"F0.wireOp",EDGE,"E7.3.29.0"),sQuery(id+"F0.wireOp",EDGE,"E7.6.29.0"),sQuery(id+"F0.wireOp",EDGE,"E7.2.30.0"),sQuery(id+"F0.wireOp",EDGE,"E7.3.30.0"),sQuery(id+"F0.wireOp",EDGE,"E7.6.30.0"),sQuery(id+"F0.wireOp",EDGE,"E7.2.31.0"),sQuery(id+"F0.wireOp",EDGE,"E7.3.31.0"),sQuery(id+"F0.wireOp",EDGE,"E7.6.31.0"),sQuery(id+"F0.wireOp",EDGE,"E7.2.32.0"),sQuery(id+"F0.wireOp",EDGE,"E7.3.32.0"),sQuery(id+"F0.wireOp",EDGE,"E7.6.32.0"),sQuery(id+"F0.wireOp",EDGE,"E7.2.33.0"),sQuery(id+"F0.wireOp",EDGE,"E7.3.33.0"),sQuery(id+"F0.wireOp",EDGE,"E7.6.33.0"),sQuery(id+"F0.wireOp",EDGE,"E7.2.34.0"),sQuery(id+"F0.wireOp",EDGE,"E7.3.34.0"),sQuery(id+"F0.wireOp",EDGE,"E7.6.34.0"),sQuery(id+"F0.wireOp",EDGE,"E7.2.35.0"),sQuery(id+"F0.wireOp",EDGE,"E7.3.35.0"),sQuery(id+"F0.wireOp",EDGE,"E7.6.35.0"),sQuery(id+"F0.wireOp",EDGE,"E7.2.36.0"),sQuery(id+"F0.wireOp",EDGE,"E7.3.36.0"),sQuery(id+"F0.wireOp",EDGE,"E7.6.36.0"),sQuery(id+"F0.wireOp",EDGE,"E7.2.37.0"),sQuery(id+"F0.wireOp",EDGE,"E7.3.37.0"),sQuery(id+"F0.wireOp",EDGE,"E7.6.37.0"),sQuery(id+"F0.wireOp",EDGE,"E7.2.38.0"),sQuery(id+"F0.wireOp",EDGE,"E7.3.38.0"),sQuery(id+"F0.wireOp",EDGE,"E7.6.38.0"),sQuery(id+"F0.wireOp",EDGE,"E7.2.39.0"),sQuery(id+"F0.wireOp",EDGE,"E7.3.39.0"),sQuery(id+"F0.wireOp",EDGE,"E7.6.39.0"),sQuery(id+"F0.wireOp",EDGE,"E7.2.40.0"),sQuery(id+"F0.wireOp",EDGE,"E7.3.40.0"),sQuery(id+"F0.wireOp",EDGE,"E7.6.40.0"),sQuery(id+"F0.wireOp",EDGE,"E7.2.41.0"),sQuery(id+"F0.wireOp",EDGE,"E7.3.41.0"),sQuery(id+"F0.wireOp",EDGE,"E7.6.41.0"),sQuery(id+"F0.wireOp",EDGE,"E7.2.42.0"),sQuery(id+"F0.wireOp",EDGE,"E7.3.42.0"),sQuery(id+"F0.wireOp",EDGE,"E7.6.42.0"),sQuery(id+"F0.wireOp",EDGE,"E7.2.43.0"),sQuery(id+"F0.wireOp",EDGE,"E7.3.43.0"),sQuery(id+"F0.wireOp",EDGE,"E7.6.43.0"),sQuery(id+"F0.wireOp",EDGE,"E7.2.44.0"),sQuery(id+"F0.wireOp",EDGE,"E7.3.44.0"),sQuery(id+"F0.wireOp",EDGE,"E7.6.44.0"),sQuery(id+"F0.wireOp",EDGE,"E7.2.45.0"),sQuery(id+"F0.wireOp",EDGE,"E7.3.45.0"),sQuery(id+"F0.wireOp",EDGE,"E7.6.45.0"),sQuery(id+"F0.wireOp",EDGE,"E7.2.46.0"),sQuery(id+"F0.wireOp",EDGE,"E7.3.46.0"),sQuery(id+"F0.wireOp",EDGE,"E7.6.46.0"),sQuery(id+"F0.wireOp",EDGE,"E7.2.47.0"),sQuery(id+"F0.wireOp",EDGE,"E7.3.47.0"),sQuery(id+"F0.wireOp",EDGE,"E7.6.47.0"),sQuery(id+"F0.wireOp",EDGE,"E7.2.48.0"),sQuery(id+"F0.wireOp",EDGE,"E7.3.48.0"),sQuery(id+"F0.wireOp",EDGE,"E7.6.48.0"),sQuery(id+"F0.wireOp",EDGE,"E7.2.49.0"),sQuery(id+"F0.wireOp",EDGE,"E7.3.49.0"),sQuery(id+"F0.wireOp",EDGE,"E7.6.49.0"),sQuery(id+"F0.wireOp",EDGE,"E8.2.50.0"),sQuery(id+"F0.wireOp",EDGE,"E8.3.50.0"),sQuery(id+"F0.wireOp",EDGE,"E8.6.50.0"),sQuery(id+"F0.wireOp",EDGE,"E8.2.51.0"),sQuery(id+"F0.wireOp",EDGE,"E8.3.51.0"),sQuery(id+"F0.wireOp",EDGE,"E8.6.51.0"),sQuery(id+"F0.wireOp",EDGE,"E8.2.52.0"),sQuery(id+"F0.wireOp",EDGE,"E8.3.52.0"),sQuery(id+"F0.wireOp",EDGE,"E8.6.52.0"),sQuery(id+"F0.wireOp",EDGE,"E8.2.53.0"),sQuery(id+"F0.wireOp",EDGE,"E8.3.53.0"),sQuery(id+"F0.wireOp",EDGE,"E8.6.53.0"),sQuery(id+"F0.wireOp",EDGE,"E8.2.54.0"),sQuery(id+"F0.wireOp",EDGE,"E8.3.54.0"),sQuery(id+"F0.wireOp",EDGE,"E8.6.54.0"),sQuery(id+"F0.wireOp",EDGE,"E8.2.55.0"),sQuery(id+"F0.wireOp",EDGE,"E8.3.55.0"),sQuery(id+"F0.wireOp",EDGE,"E8.6.55.0"),sQuery(id+"F0.wireOp",EDGE,"E8.2.56.0"),sQuery(id+"F0.wireOp",EDGE,"E8.3.56.0"),sQuery(id+"F0.wireOp",EDGE,"E8.6.56.0"),sQuery(id+"F0.wireOp",EDGE,"E8.2.57.0"),sQuery(id+"F0.wireOp",EDGE,"E8.3.57.0"),sQuery(id+"F0.wireOp",EDGE,"E8.6.57.0"),sQuery(id+"F0.wireOp",EDGE,"E8.2.58.0"),sQuery(id+"F0.wireOp",EDGE,"E8.3.58.0"),sQuery(id+"F0.wireOp",EDGE,"E8.6.58.0"),sQuery(id+"F0.wireOp",EDGE,"E8.2.59.0"),sQuery(id+"F0.wireOp",EDGE,"E8.3.59.0"),sQuery(id+"F0.wireOp",EDGE,"E8.6.59.0"),sQuery(id+"F0.wireOp",EDGE,"E10")])],"isStart":false});
            var sketch = newSketch(context, id + "F4", { "sketchPlane" : qUnion([Q0])});
            skSolve(sketch);
        }
        {
            var Q0;
            {var subQ5=sQuery(id+"F0.wireOp",EDGE,"E2");Q0=makeQuery(id+"F4.imprint","IMPRINT",FACE,{"disambiguationData":[TD([[makeQuery(id+"F4.imprint","IMPRINT",EDGE,{"derivedFrom":makeQuery(id+"F1.opExtrude","CAP_EDGE",EDGE,{"disambiguationData":[OSD([subQ5])],"isStart":false})}),-1.0]])]});}
            extrude(context, id + "F5", {"entities" : qUnion([Q0]), "operationType" : NewBodyOperationType.REMOVE, "endBound" : BoundingType.THROUGH_ALL, "oppositeDirection" : true, "depth" : 25.4 * mm, "offsetDistance" : 25.4 * mm});
        }
    });
